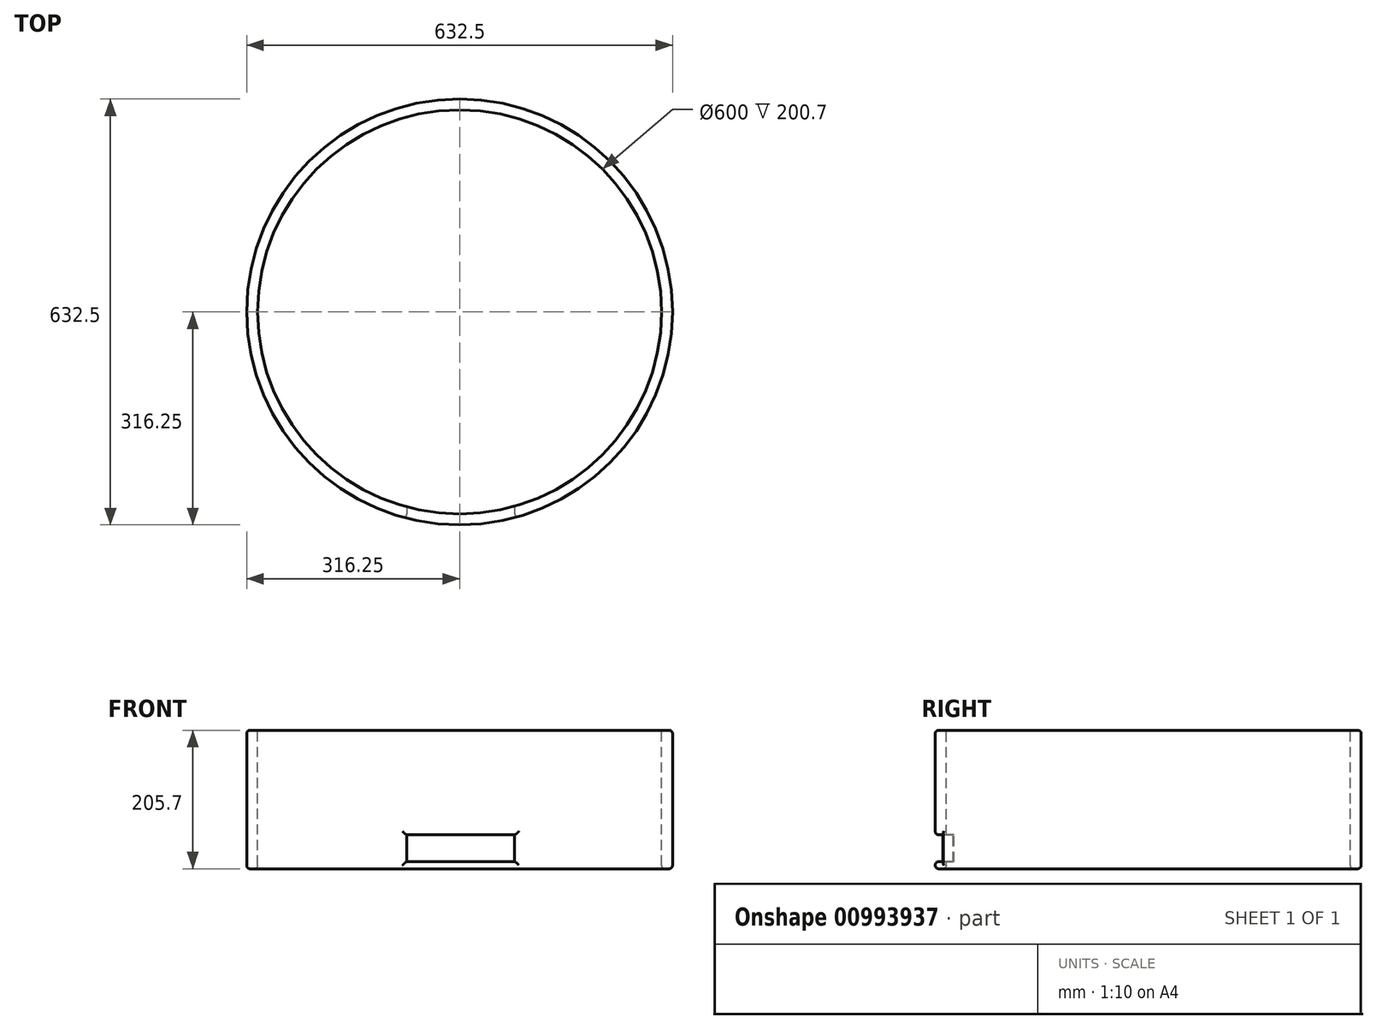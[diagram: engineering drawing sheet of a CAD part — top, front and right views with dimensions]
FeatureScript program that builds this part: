
annotation { "Feature Type Name" : "Feature", "Feature Type Description" : "" }
export const myFeature = defineFeature(function(context is Context, id is Id, definition is map)
    precondition{}
    {
        {
            var Q0;
            Q0=qCreatedBy(makeId("Top.planeOp"),FACE);
            var sketch = newSketch(context, id + "F0", { "sketchPlane" : qUnion([Q0])});
            skCircle(sketch, "E0", {"center": v(0, 0) * mm, "radius": 316.25 * mm});
            skSolve(sketch);
        }
        {
            var Q0;
            Q0 = qSketchRegion(id + "F0", true);
            extrude(context, id + "F1", {"entities" : qUnion([Q0]), "depth" : 205.7 * mm, "offsetDistance" : 25 * mm});
        }
        {
            var Q0;
            Q0=makeQuery(id+"F1.opExtrude","CAP_FACE",FACE,{"disambiguationData":[OSD([sQuery(id+"F0.wireOp",EDGE,"E0")])],"isStart":false});
            var sketch = newSketch(context, id + "F2", { "sketchPlane" : qUnion([Q0])});
            skCircle(sketch, "E1", {"center": v(0, 0) * mm, "radius": 300 * mm});
            skSolve(sketch);
        }
        {
            var Q0;
            Q0=makeQuery(id+"F2.imprint","IMPRINT",FACE,{"disambiguationData":[TD([[makeQuery(id+"F2.imprint","IMPRINT",EDGE,{"derivedFrom":sQuery(id+"F2.wireOp",EDGE,"E1")}),1.0]])]});
            extrude(context, id + "F3", {"entities" : qUnion([Q0]), "operationType" : NewBodyOperationType.REMOVE, "oppositeDirection" : true, "depth" : 631 * mm, "offsetDistance" : 25 * mm});
        }
        {
            var Q0;
            Q0=qCreatedBy(makeId("Front.planeOp"),FACE);
            cPlane(context, id + "F4", {"entities" : qUnion([Q0]), "cplaneType" : CPlaneType.OFFSET, "offset" : 645.54 * mm, "width" : 150 * mm, "height" : 150 * mm});
        }
        {
            var Q0;
            Q0=qCreatedBy(id+"F4.planeOp",FACE);
            var sketch = newSketch(context, id + "F5", { "sketchPlane" : qUnion([Q0])});
            skLineSegment(sketch, "E2.bottom", {"start": v(-78.3, 10.46) * mm, "end": v(81.7, 10.46) * mm});
            skLineSegment(sketch, "E2.top", {"start": v(-78.3, 50.46) * mm, "end": v(81.7, 50.46) * mm});
            skLineSegment(sketch, "E2.left", {"start": v(-78.3, 10.46) * mm, "end": v(-78.3, 50.46) * mm});
            skLineSegment(sketch, "E2.right", {"start": v(81.7, 10.46) * mm, "end": v(81.7, 50.46) * mm});
            skSolve(sketch);
        }
        {
            var Q0;
            Q0 = qSketchRegion(id + "F5", true);
            extrude(context, id + "F6", {"entities" : qUnion([Q0]), "operationType" : NewBodyOperationType.REMOVE, "oppositeDirection" : true, "depth" : 796.12 * mm, "offsetDistance" : 25 * mm});
        }
        {
            var Q0;
            Q0=makeQuery(id+"F1.opExtrude","CAP_EDGE",EDGE,{"disambiguationData":[OSD([sQuery(id+"F0.wireOp",EDGE,"E0")])],"isStart":false});
            var Q1;
            Q1=makeQuery(id+"F3.boolean.opBoolean","COPY",EDGE,{"derivedFrom":makeQuery(id+"F3.opExtrude","CAP_EDGE",EDGE,{"disambiguationData":[OSD([sQuery(id+"F2.wireOp",EDGE,"E1")])],"isStart":true})});
            var Q2;
            Q2=makeQuery(id+"F6.boolean.opBoolean","INTERSECT",EDGE,{"derivedFrom":[makeQuery(id+"F1.opExtrude","SWEPT_FACE",FACE,{"disambiguationData":[OSD([sQuery(id+"F0.wireOp",EDGE,"E0")])]}),makeQuery(id+"F6.opExtrude","SWEPT_FACE",FACE,{"disambiguationData":[OSD([sQuery(id+"F5.wireOp",EDGE,"E2.top")])]})]});
            var Q3;
            Q3=makeQuery(id+"F6.boolean.opBoolean","INTERSECT",EDGE,{"derivedFrom":[makeQuery(id+"F1.opExtrude","SWEPT_FACE",FACE,{"disambiguationData":[OSD([sQuery(id+"F0.wireOp",EDGE,"E0")])]}),makeQuery(id+"F6.opExtrude","SWEPT_FACE",FACE,{"disambiguationData":[OSD([sQuery(id+"F5.wireOp",EDGE,"E2.right")])]})]});
            var Q4;
            Q4=makeQuery(id+"F6.boolean.opBoolean","INTERSECT",EDGE,{"derivedFrom":[makeQuery(id+"F1.opExtrude","SWEPT_FACE",FACE,{"disambiguationData":[OSD([sQuery(id+"F0.wireOp",EDGE,"E0")])]}),makeQuery(id+"F6.opExtrude","SWEPT_FACE",FACE,{"disambiguationData":[OSD([sQuery(id+"F5.wireOp",EDGE,"E2.left")])]})]});
            var Q5;
            Q5=makeQuery(id+"F6.boolean.opBoolean","INTERSECT",EDGE,{"derivedFrom":[makeQuery(id+"F1.opExtrude","SWEPT_FACE",FACE,{"disambiguationData":[OSD([sQuery(id+"F0.wireOp",EDGE,"E0")])]}),makeQuery(id+"F6.opExtrude","SWEPT_FACE",FACE,{"disambiguationData":[OSD([sQuery(id+"F5.wireOp",EDGE,"E2.bottom")])]})]});
            var Q6;
            Q6=makeQuery(id+"F1.opExtrude","CAP_EDGE",EDGE,{"disambiguationData":[OSD([sQuery(id+"F0.wireOp",EDGE,"E0")])],"isStart":true});
            var Q7;
            Q7=makeQuery(id+"F3.boolean.opBoolean","INTERSECT",EDGE,{"derivedFrom":[makeQuery(id+"F1.opExtrude","CAP_FACE",FACE,{"disambiguationData":[OSD([sQuery(id+"F0.wireOp",EDGE,"E0")])],"isStart":true}),makeQuery(id+"F3.opExtrude","SWEPT_FACE",FACE,{"disambiguationData":[OSD([sQuery(id+"F2.wireOp",EDGE,"E1")])]})]});
            fillet(context, id + "F7", {"entities" : qUnion([Q0, Q1, Q2, Q3, Q4, Q5, Q6, Q7]), "radius" : 5 * mm, "tangentPropagation" : true, "allowEdgeOverflow" : false});
        }
    });
